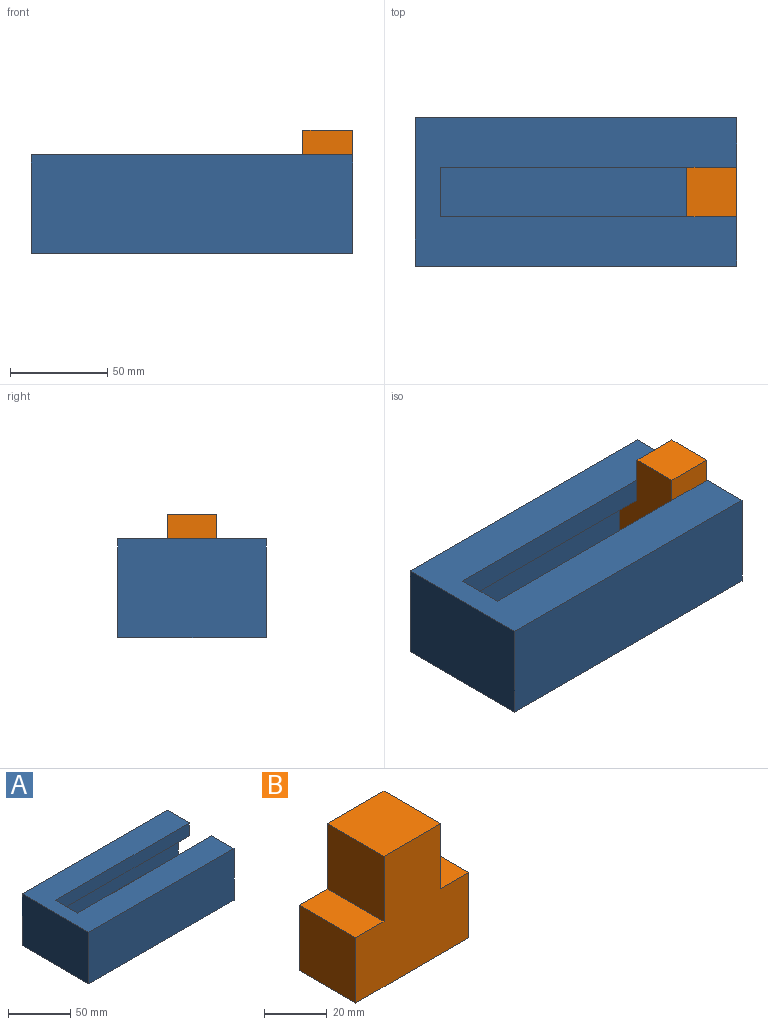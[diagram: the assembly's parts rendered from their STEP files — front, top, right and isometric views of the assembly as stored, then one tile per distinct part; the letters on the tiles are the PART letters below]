
ASSEMBLY  parts=2 mates=1
PART A: 14 faces, bbox 165.1x76.2x50.8 mm
  f0: plane 76.2x50.8mm, normal (1,0,0), area 2258.1mm2, adj f1,f2,f3,f4,f5,f6,f7,f8
  f1: plane 165.1x50.8mm, normal (0,1,0), area 8387.1mm2, adj f0,f3,f4,f12
  f2: plane 165.1x50.8mm, normal (0,-1,0), area 8387.1mm2, adj f0,f3,f4,f12
  f3: plane 165.1x76.2mm, normal (0,0,1), area 8709.7mm2, adj f0,f1,f2,f5,f6,f12,f13
  f4: plane 165.1x76.2mm, normal (0,0,-1), area 12580.6mm2, adj f0,f1,f2,f12
  f5: plane 152.4x12.7mm, normal (0,1,0), area 1935.5mm2, adj f0,f3,f7,f13
  f6: plane 152.4x12.7mm, normal (0,-1,0), area 1935.5mm2, adj f0,f3,f11,f13
  f7: plane 152.4x12.7mm, normal (0,0,-1), area 1935.5mm2, adj f0,f5,f8,f13
  f8: plane 152.4x25.4mm, normal (0,1,0), area 3871mm2, adj f0,f7,f9,f13
  f9: plane 152.4x50.8mm, normal (0,0,1), area 7741.9mm2, adj f0,f8,f10,f13
  f10: plane 152.4x25.4mm, normal (0,-1,0), area 3871mm2, adj f0,f9,f11,f13
  f11: plane 152.4x12.7mm, normal (0,0,-1), area 1935.5mm2, adj f0,f6,f10,f13
  f12: plane 76.2x50.8mm, normal (-1,0,0), area 3871mm2, adj f1,f2,f3,f4
  f13: plane 50.8x38.1mm, normal (1,0,0), area 1612.9mm2, adj f3,f5,f6,f7,f8,f9,f10,f11
PART B: 10 faces, bbox 50.8x25.4x50.8 mm
  f0: plane 25.4x12.7mm, normal (0,0,1), area 322.6mm2, adj f1,f7,f8,f9
  f1: plane 25.4x25.4mm, normal (1,0,0), area 645.2mm2, adj f0,f2,f8,f9
  f2: plane 25.4x25.4mm, normal (0,0,1), area 645.2mm2, adj f1,f3,f8,f9
  f3: plane 25.4x25.4mm, normal (-1,0,0), area 645.2mm2, adj f2,f4,f8,f9
  f4: plane 25.4x12.7mm, normal (0,0,1), area 322.6mm2, adj f3,f5,f8,f9
  f5: plane 25.4x25.4mm, normal (-1,0,0), area 645.2mm2, adj f4,f6,f8,f9
  f6: plane 50.8x25.4mm, normal (0,0,-1), area 1290.3mm2, adj f5,f7,f8,f9
  f7: plane 25.4x25.4mm, normal (1,0,0), area 645.2mm2, adj f0,f6,f8,f9
  f8: plane 50.8x50.8mm, normal (0,-1,0), area 1935.5mm2, adj f0,f1,f2,f3,f4,f5,f6,f7
  f9: plane 50.8x50.8mm, normal (0,1,0), area 1935.5mm2, adj f0,f1,f2,f3,f4,f5,f6,f7
PLACE A t=(-3.28,1.39,-41.8)mm fixed
PLACE B rot(axis=(0,0,-1),90deg) t=(81.42,6.57,-16.4)mm
MATE slider A.f0 <-> B.f9  axis (1,0,0) through (81.56,-18.83,-29.1)mm
